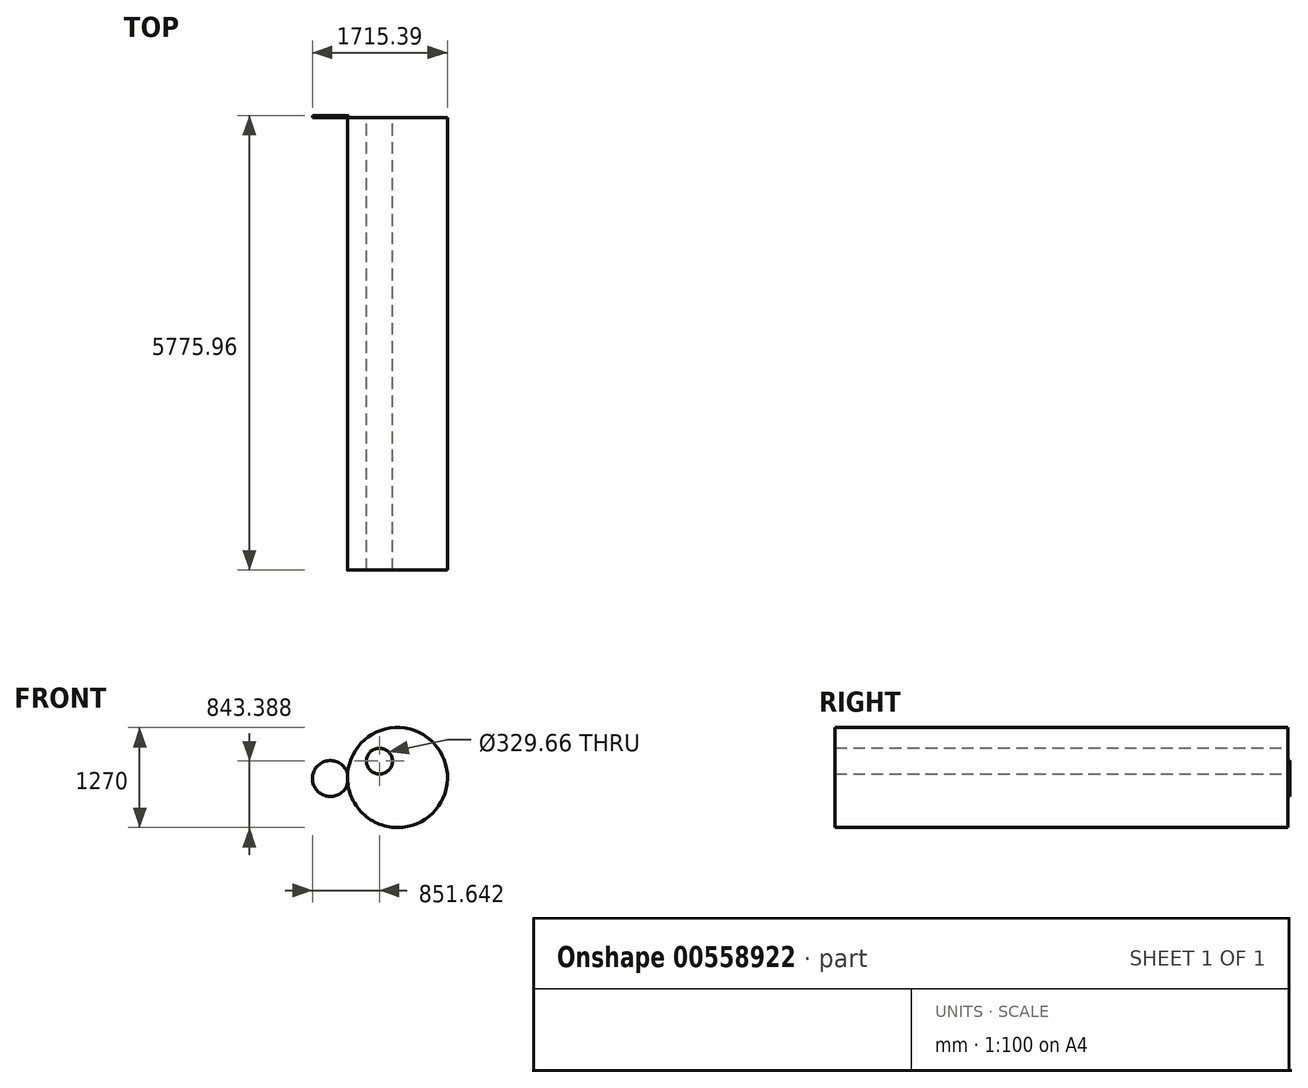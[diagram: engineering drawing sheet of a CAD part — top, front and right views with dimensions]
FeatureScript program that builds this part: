
annotation { "Feature Type Name" : "Feature", "Feature Type Description" : "" }
export const myFeature = defineFeature(function(context is Context, id is Id, definition is map)
    precondition{}
    {
        {
            var Q0;
            Q0=qCreatedBy(makeId("Front.planeOp"),FACE);
            var sketch = newSketch(context, id + "F0", { "sketchPlane" : qUnion([Q0])});
            skCircle(sketch, "E0", {"center": v(-91, 22.9) * mm, "radius": 635 * mm});
            skCircle(sketch, "E1", {"center": v(-319.75, 231.3) * mm, "radius": 164.83 * mm});
            skSolve(sketch);
        }
        {
            var Q0;
            Q0 = qSketchRegion(id + "F0", true);
            extrude(context, id + "F1", {"entities" : qUnion([Q0]), "depth" : 5750.56 * mm, "offsetDistance" : 25.4 * mm});
        }
        {
            var Q0;
            Q0=makeQuery(id+"F1.opExtrude","CAP_FACE",FACE,{"disambiguationData":[OSD([sQuery(id+"F0.wireOp",EDGE,"E0")])],"isStart":true});
            var sketch = newSketch(context, id + "F2", { "sketchPlane" : qUnion([Q0])});
            skCircle(sketch, "E2", {"center": v(943.09, 9.79) * mm, "radius": 228.3 * mm});
            skSolve(sketch);
        }
        {
            var Q0;
            {var subQ0=sQuery(id+"F2.wireOp",EDGE,"E2");var subQ1=makeQuery(id+"F1.opExtrude","CAP_EDGE",EDGE,{"disambiguationData":[OSD([sQuery(id+"F0.wireOp",EDGE,"E0")])],"isStart":true});var subQ2=makeQuery(id+"F2.imprint","INTERSECT",VERTEX,{"disambiguationData":[OD(0.0)],"derivedFrom":[subQ1,subQ0]});Q0=makeQuery(id+"F2.imprint","IMPRINT",FACE,{"disambiguationData":[TD([[makeQuery(id+"F2.imprint","IMPRINT",EDGE,{"disambiguationData":[TD([[subQ2,1.0]])],"derivedFrom":subQ0}),1.0]])]});}
            var Q1;
            {var subQ0=sQuery(id+"F2.wireOp",EDGE,"E2");var subQ1=makeQuery(id+"F1.opExtrude","CAP_EDGE",EDGE,{"disambiguationData":[OSD([sQuery(id+"F0.wireOp",EDGE,"E0")])],"isStart":true});var subQ2=makeQuery(id+"F2.imprint","INTERSECT",VERTEX,{"disambiguationData":[OD(0.0)],"derivedFrom":[subQ1,subQ0]});Q1=makeQuery(id+"F2.imprint","IMPRINT",FACE,{"disambiguationData":[TD([[makeQuery(id+"F2.imprint","IMPRINT",EDGE,{"disambiguationData":[TD([[subQ2,-1.0]])],"derivedFrom":subQ0}),1.0]])]});}
            extrude(context, id + "F3", {"entities" : qUnion([Q0, Q1]), "operationType" : NewBodyOperationType.ADD, "depth" : 25.4 * mm, "offsetDistance" : 25.4 * mm});
        }
        {
            var Q0;
            Q0 = qSketchRegion(id + "F0", true);
            extrude(context, id + "F4", {"entities" : qUnion([Q0]), "operationType" : NewBodyOperationType.ADD, "depth" : 25.4 * mm, "offsetDistance" : 25.4 * mm});
        }
    });
